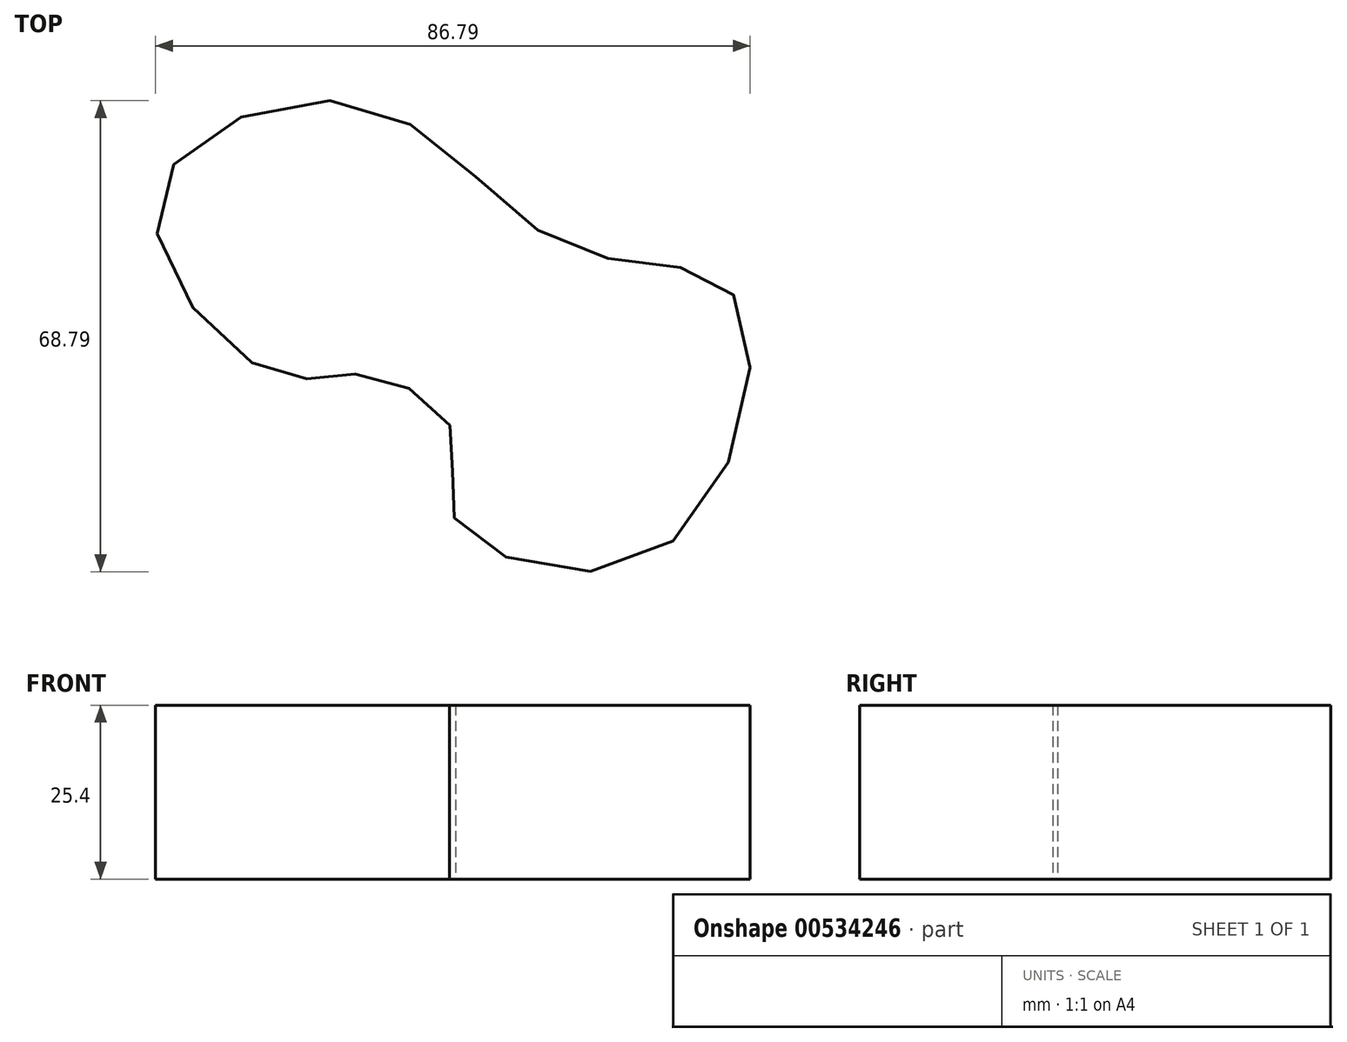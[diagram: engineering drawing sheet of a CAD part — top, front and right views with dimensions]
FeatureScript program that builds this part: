
annotation { "Feature Type Name" : "Feature", "Feature Type Description" : "" }
export const myFeature = defineFeature(function(context is Context, id is Id, definition is map)
    precondition{}
    {
        {
            var Q0;
            Q0=qCreatedBy(makeId("Top.planeOp"),FACE);
            var sketch = newSketch(context, id + "F0", { "sketchPlane" : qUnion([Q0])});
            skFitSpline(sketch, "E0", {"points": [v(0, -32.34) * mm, v(29.7, -37.3) * mm, v(40.94, 0) * mm, v(16.94, 7.07) * mm, v(-13.03, 27.89) * mm, v(-43.36, 14.23) * mm, v(-26.68, -11.16) * mm, v(-12.67, -11.43) * mm, v(0, -20.43) * mm, v(0, -32.34) * mm]});
            skSolve(sketch);
        }
        {
            var Q0;
            Q0 = qSketchRegion(id + "F0", true);
            extrude(context, id + "F1", {"entities" : qUnion([Q0]), "depth" : 25.4 * mm, "offsetDistance" : 25.4 * mm});
        }
    });
